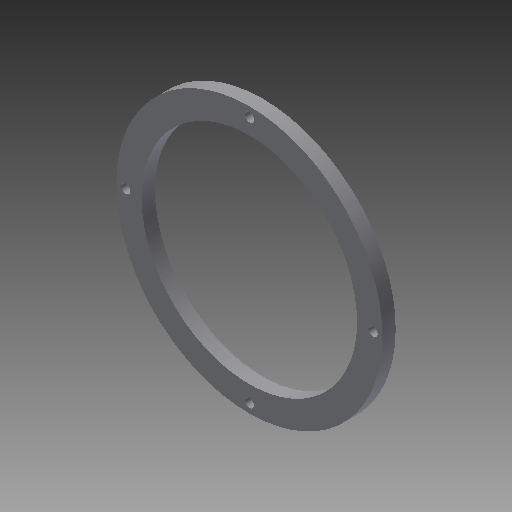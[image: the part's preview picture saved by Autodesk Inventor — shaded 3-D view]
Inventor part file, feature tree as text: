
AUTODESK INVENTOR PART (.ipt)
format: ipt  version: 2017 (Build 210142000, 142)  size: 99,328 bytes
history: native  units: mm
features: extrude x1, sketch x1
ambient origin geometry x8: Origin, YZ Plane, XZ Plane, XY Plane, X Axis, Y Axis, Z Axis, Center Point
bodies: Solid1 (feature_tree)
feature tree (2):
  extrude  "Extrusion1"  Depth=5.0mm
  sketch  "Sketch1"  dims[d0=81.0mm d1=86.0mm d2=100.0mm d3=3.5mm d4=40.0mm d6=360.0deg d8=5.0mm d9=0.0mm]
